# Revit family: Wall_Capping-K2_Stone-Crown_Isle_Granite-1
name_source: partatom
category: Profiles
revit_build: Autodesk Revit Architecture 2013 (Build: 20130531_2115(x64)
units: mm (PartAtom-declared; Revit-internal decimal feet)

## types (1)
- Crown Isle Granite
    Description = Our Crown Isle Granite wall cap has a cut top, bottom and flamed sides.
    LEED = https://www.k2stone.com
    Manufacturer = K2 Stone
    Max Length = 4' - 0"
    Max Thickness = 0' - 8"
    Max Width = 2' - 0"
    Min Length = 0' - 3"
    Min Thickness = 0' - 2"
    Min Width = 0' - 3"
    Model = Crown Isle Granite Capping
    Product Documentation Link = https://www.k2stone.com
    Product Page URL = https://www.k2stone.com
    Requested Thickness = 0' - 2"
    Requested Width = 0' - 4"
    Thickness = 0' - 2"
    Type Comments = Capping
    URL = https://www.k2stone.com
    Width = 0' - 4"

## geometry (parser evidence)
native form markers: Blend x2, Sweep x1
no freeform markers — native parametric forms only
